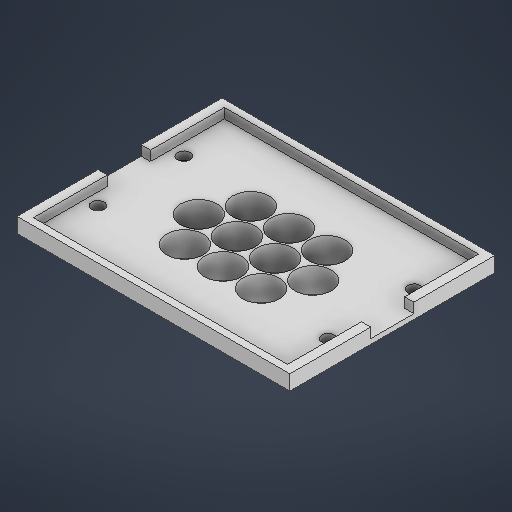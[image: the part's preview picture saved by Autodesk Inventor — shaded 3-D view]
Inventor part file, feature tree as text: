
AUTODESK INVENTOR PART (.ipt)
format: ipt  version: 2025.2 (Build 292293000, 293)  size: 610,816 bytes
history: native  units: mm
features: extrude x5, sketch x5, projected_geometry x2
ambient origin geometry x8: Origin, YZ Plane, XZ Plane, XY Plane, X Axis, Y Axis, Z Axis, Center Point
bodies: Solid1 (feature_tree)
feature tree (12):
  extrude  "Extrusion1"  Depth=1.0mm
  extrude  "Extrusion2"  Depth=1.0mm
  extrude  "Extrusion3"  Depth=1.0mm
  extrude  "Extrusion4"  Depth=24.0mm
  extrude  "Extrusion5"  Depth=3.0mm
  sketch  "Sketch1"  dims[d0=22.0mm d1=1.0mm]
  sketch  "Sketch2"  dims[d2=22.0mm d3=1.0mm]
  sketch  "Sketch3"  dims[d4=22.0mm d5=1.0mm]
  projected_geometry  "Projected Loop1"
  sketch  "Sketch4"  dims[d6=22.0mm d7=24.0mm]
  projected_geometry  "Projected Loop2"
  sketch  "Sketch5"  dims[d8=24.0mm d9=24.0mm d10=24.0mm d11=22.0mm d12=22.0mm d16=22.0mm d17=22.0mm d19=24.0mm d21=24.0mm d22=24.0mm d23=24.0mm d25=26.0mm d27=26.0mm d28=26.0mm d29=26.0mm d30=26.0mm d31=26.0mm d32=26.0mm d33=26.0mm d34=15.0mm d35=0.0mm d36=115.3mm d37=153.4mm d38=5.0mm d39=0.0mm d44=6.0mm d45=3.0mm d46=0.0mm d47=0.0mm d56=7.73mm d57=7.73mm d58=7.73mm d59=7.73mm d60=0.0mm d61=0.0mm d62=7.228mm d63=31.75mm d64=7.228mm d65=7.228mm d66=31.75mm d67=24.0mm d71=24.0mm d72=22.0mm d73=22.0mm d74=0.0mm d75=0.0mm]
